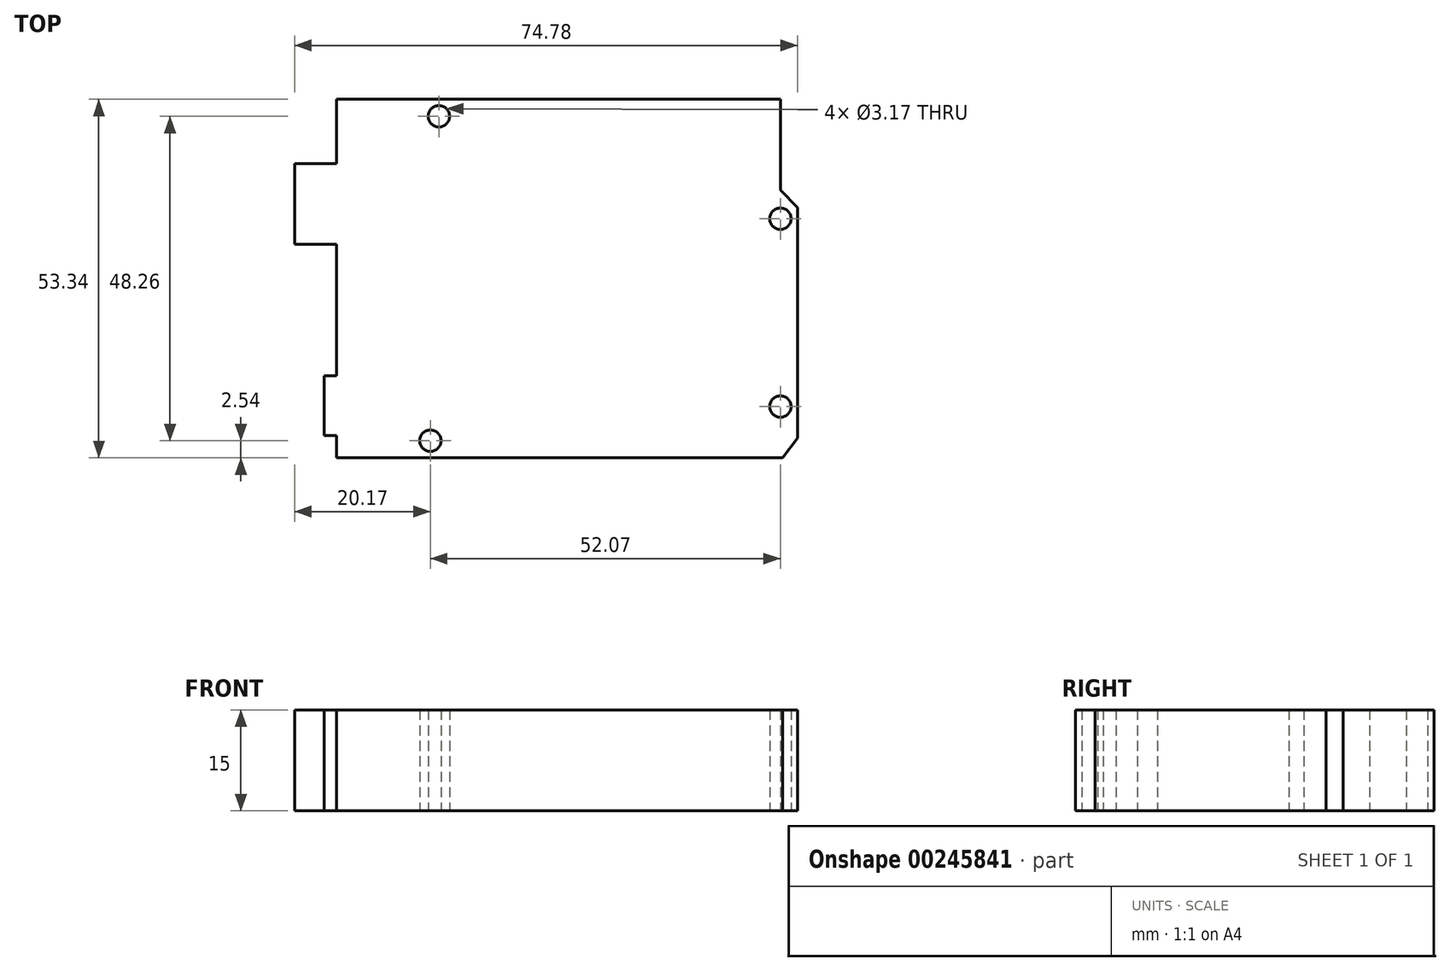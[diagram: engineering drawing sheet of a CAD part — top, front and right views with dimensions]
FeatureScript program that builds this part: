
annotation { "Feature Type Name" : "Feature", "Feature Type Description" : "" }
export const myFeature = defineFeature(function(context is Context, id is Id, definition is map)
    precondition{}
    {
        {
            var Q0;
            Q0=qCreatedBy(makeId("Top.planeOp"),FACE);
            var sketch = newSketch(context, id + "F0", { "sketchPlane" : qUnion([Q0])});
            skLineSegment(sketch, "E0.bottom", {"start": v(32.08, -26.67) * mm, "end": v(-34.3, -26.67) * mm});
            skLineSegment(sketch, "E0.top", {"start": v(31.75, 26.67) * mm, "end": v(-34.3, 26.67) * mm});
            skLineSegment(sketch, "E0.left", {"start": v(34.3, -23.76) * mm, "end": v(34.3, 10.58) * mm});
            skLineSegment(sketch, "E0.right", {"start": v(-34.3, -26.67) * mm, "end": v(-34.3, 26.67) * mm});
            skPoint(sketch, "E0.middle", {"position": v(0, 0) * mm});
            skCircle(sketch, "E1", {"center": v(-20.32, -24.13) * mm, "radius": 1.59 * mm});
            skCircle(sketch, "E2", {"center": v(-19.05, 24.13) * mm, "radius": 1.59 * mm});
            skCircle(sketch, "E3", {"center": v(31.75, 8.89) * mm, "radius": 1.59 * mm});
            skCircle(sketch, "E4", {"center": v(31.75, -19.05) * mm, "radius": 1.59 * mm});
            skLineSegment(sketch, "E5", {"start": v(31.75, 26.67) * mm, "end": v(31.75, 13.14) * mm});
            skLineSegment(sketch, "E6", {"start": v(34.3, 10.58) * mm, "end": v(31.75, 13.14) * mm});
            skLineSegment(sketch, "E7", {"start": v(34.3, -23.76) * mm, "end": v(32.08, -26.67) * mm});
            skPoint(sketch, "E8.orphan", {"position": v(34.3, -26.67) * mm});
            skPoint(sketch, "E9.orphan", {"position": v(34.3, 26.67) * mm});
            skLineSegment(sketch, "E10", {"start": v(-34.3, 17.07) * mm, "end": v(-40.5, 17.07) * mm});
            skLineSegment(sketch, "E11", {"start": v(-40.5, 17.07) * mm, "end": v(-40.5, 5.07) * mm});
            skLineSegment(sketch, "E12", {"start": v(-40.5, 5.07) * mm, "end": v(-34.3, 5.07) * mm});
            skLineSegment(sketch, "E13", {"start": v(-34.3, -14.47) * mm, "end": v(-36.1, -14.47) * mm});
            skLineSegment(sketch, "E14", {"start": v(-36.1, -14.47) * mm, "end": v(-36.1, -23.37) * mm});
            skLineSegment(sketch, "E15", {"start": v(-36.1, -23.37) * mm, "end": v(-34.3, -23.37) * mm});
            skSolve(sketch);
        }
        {
            var Q0;
            {var subQ3=sQuery(id+"F0.wireOp",EDGE,"E0.bottom");Q0=makeQuery(id+"F0.imprint","IMPRINT",FACE,{"disambiguationData":[TD([[makeQuery(id+"F0.imprint","IMPRINT",EDGE,{"derivedFrom":subQ3}),-1.0]])]});}
            var Q1;
            {var subQ0=sQuery(id+"F0.wireOp",EDGE,"E10");Q1=makeQuery(id+"F0.imprint","IMPRINT",FACE,{"disambiguationData":[TD([[makeQuery(id+"F0.imprint","IMPRINT",EDGE,{"derivedFrom":subQ0}),1.0]])]});}
            var Q2;
            {var subQ0=sQuery(id+"F0.wireOp",EDGE,"E13");Q2=makeQuery(id+"F0.imprint","IMPRINT",FACE,{"disambiguationData":[TD([[makeQuery(id+"F0.imprint","IMPRINT",EDGE,{"derivedFrom":subQ0}),1.0]])]});}
            extrude(context, id + "F1", {"entities" : qUnion([Q0, Q1, Q2]), "depth" : 15 * mm});
        }
    });
